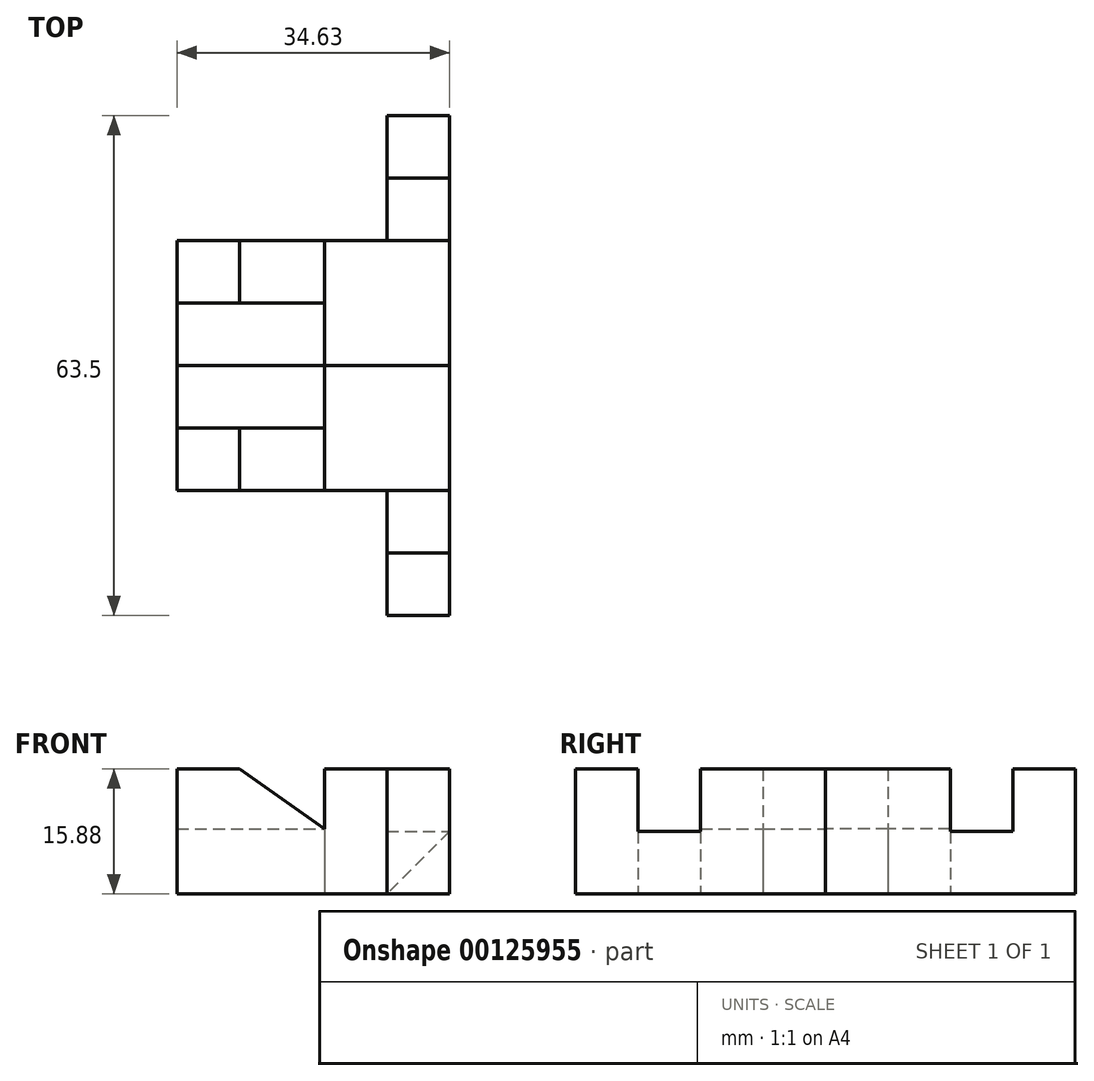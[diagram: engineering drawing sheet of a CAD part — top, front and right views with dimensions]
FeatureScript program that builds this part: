
annotation { "Feature Type Name" : "Feature", "Feature Type Description" : "" }
export const myFeature = defineFeature(function(context is Context, id is Id, definition is map)
    precondition{}
    {
        {
            var Q0;
            Q0=qCreatedBy(makeId("Top.planeOp"),FACE);
            var sketch = newSketch(context, id + "F0", { "sketchPlane" : qUnion([Q0])});
            skLineSegment(sketch, "E0.bottom", {"start": v(0, 0) * mm, "end": v(34.63, 0) * mm});
            skLineSegment(sketch, "E0.right", {"start": v(34.63, 0) * mm, "end": v(34.63, 31.75) * mm});
            skLineSegment(sketch, "E1", {"start": v(0, 15.88) * mm, "end": v(34.63, 15.88) * mm});
            skLineSegment(sketch, "E2", {"start": v(7.94, 15.88) * mm, "end": v(7.94, 7.94) * mm});
            skLineSegment(sketch, "E3", {"start": v(0, 15.88) * mm, "end": v(0, 0) * mm});
            skLineSegment(sketch, "E4", {"start": v(26.7, 31.75) * mm, "end": v(34.63, 31.75) * mm});
            skLineSegment(sketch, "E5", {"start": v(26.7, 23.81) * mm, "end": v(34.63, 23.81) * mm});
            skLineSegment(sketch, "E6", {"start": v(18.75, 15.88) * mm, "end": v(18.75, 0) * mm});
            skLineSegment(sketch, "E7", {"start": v(26.7, 31.75) * mm, "end": v(26.7, 15.88) * mm});
            skLineSegment(sketch, "E8", {"start": v(0, 7.94) * mm, "end": v(18.75, 7.94) * mm});
            skLineSegment(sketch, "E9", {"start": v(0, -6.14) * mm, "end": v(62.24, -6.14) * mm});
            skSolve(sketch);
        }
        {
            var Q0;
            {var subQ1=sQuery(id+"F0.wireOp",EDGE,"E0.right");var subQ4=sQuery(id+"F0.wireOp",EDGE,"E0.bottom");var subQ5=makeQuery(id+"F0.imprint","INTERSECT",VERTEX,{"derivedFrom":[subQ4,subQ1]});Q0=makeQuery(id+"F0.imprint","IMPRINT",FACE,{"disambiguationData":[TD([[makeQuery(id+"F0.imprint","IMPRINT",EDGE,{"disambiguationData":[TD([[subQ5,1.0]])],"derivedFrom":subQ4}),1.0]])]});}
            var Q1;
            {var subQ3=sQuery(id+"F0.wireOp",EDGE,"E2");Q1=makeQuery(id+"F0.imprint","IMPRINT",FACE,{"disambiguationData":[TD([[makeQuery(id+"F0.imprint","IMPRINT",EDGE,{"derivedFrom":subQ3}),-1.0]])]});}
            var Q2;
            {var subQ0=sQuery(id+"F0.wireOp",EDGE,"E4");Q2=makeQuery(id+"F0.imprint","IMPRINT",FACE,{"disambiguationData":[TD([[makeQuery(id+"F0.imprint","IMPRINT",EDGE,{"derivedFrom":subQ0}),-1.0]])]});}
            var Q3;
            {var subQ0=sQuery(id+"F0.wireOp",EDGE,"E2");Q3=makeQuery(id+"F0.imprint","IMPRINT",FACE,{"disambiguationData":[TD([[makeQuery(id+"F0.imprint","IMPRINT",EDGE,{"derivedFrom":subQ0}),1.0]])]});}
            var Q4;
            {var subQ3=sQuery(id+"F0.wireOp",EDGE,"E5");Q4=makeQuery(id+"F0.imprint","IMPRINT",FACE,{"disambiguationData":[TD([[makeQuery(id+"F0.imprint","IMPRINT",EDGE,{"derivedFrom":subQ3}),-1.0]])]});}
            extrude(context, id + "F1", {"entities" : qUnion([Q0, Q1, Q2, Q3, Q4]), "depth" : 15.88 * mm});
        }
        {
            var Q0;
            {var subQ1=sQuery(id+"F0.wireOp",EDGE,"E0.bottom");var subQ5=sQuery(id+"F0.wireOp",EDGE,"E3");var subQ6=makeQuery(id+"F0.imprint","INTERSECT",VERTEX,{"derivedFrom":[subQ1,subQ5]});Q0=makeQuery(id+"F0.imprint","IMPRINT",FACE,{"disambiguationData":[TD([[makeQuery(id+"F0.imprint","IMPRINT",EDGE,{"disambiguationData":[TD([[subQ6,-1.0]])],"derivedFrom":subQ1}),1.0]])]});}
            extrude(context, id + "F2", {"entities" : qUnion([Q0]), "depth" : 8.25 * mm});
        }
        {
            var Q0;
            Q0=makeQuery(id+"F1.opExtrude","SWEPT_FACE",FACE,{"disambiguationData":[OSD([sQuery(id+"F0.wireOp",EDGE,"E8")])]});
            var sketch = newSketch(context, id + "F3", { "sketchPlane" : qUnion([Q0])});
            skLineSegment(sketch, "E10.0", {"start": v(0, 15.88) * mm, "end": v(18.75, 15.88) * mm});
            skLineSegment(sketch, "E11.0", {"start": v(0, 8.26) * mm, "end": v(18.75, 8.26) * mm});
            skLineSegment(sketch, "E12", {"start": v(7.94, 15.88) * mm, "end": v(7.94, 8.26) * mm});
            skLineSegment(sketch, "E13", {"start": v(7.94, 15.88) * mm, "end": v(18.75, 8.26) * mm});
            skSolve(sketch);
        }
        {
            var Q0;
            {var subQ3=sQuery(id+"F3.wireOp",EDGE,"E13");Q0=makeQuery(id+"F3.imprint","IMPRINT",FACE,{"disambiguationData":[TD([[makeQuery(id+"F3.imprint","IMPRINT",EDGE,{"derivedFrom":subQ3}),1.0]])]});}
            extrude(context, id + "F4", {"entities" : qUnion([Q0]), "operationType" : NewBodyOperationType.REMOVE, "oppositeDirection" : true, "depth" : 25.4 * mm});
        }
        {
            var Q0;
            Q0=makeQuery(id+"F1.opExtrude","SWEPT_FACE",FACE,{"disambiguationData":[OSD([sQuery(id+"F0.wireOp",EDGE,"E0.right")])]});
            var sketch = newSketch(context, id + "F5", { "sketchPlane" : qUnion([Q0])});
            skLineSegment(sketch, "E14.0", {"start": v(31.75, 0) * mm, "end": v(15.87, 0) * mm});
            skLineSegment(sketch, "E15.0", {"start": v(0, 15.88) * mm, "end": v(31.75, 15.88) * mm});
            skLineSegment(sketch, "E16", {"start": v(15.87, 0) * mm, "end": v(15.87, 15.88) * mm});
            skLineSegment(sketch, "E17", {"start": v(23.81, 15.88) * mm, "end": v(23.81, 0) * mm});
            skLineSegment(sketch, "E18", {"start": v(15.87, 7.94) * mm, "end": v(23.81, 7.94) * mm});
            skSolve(sketch);
        }
        {
            var Q0;
            {var subQ5=sQuery(id+"F5.wireOp",EDGE,"E18");Q0=makeQuery(id+"F5.imprint","IMPRINT",FACE,{"disambiguationData":[TD([[makeQuery(id+"F5.imprint","IMPRINT",EDGE,{"derivedFrom":subQ5}),1.0]])]});}
            extrude(context, id + "F6", {"entities" : qUnion([Q0]), "operationType" : NewBodyOperationType.REMOVE, "oppositeDirection" : true, "depth" : 25.4 * mm});
        }
        {
            var Q0;
            Q0=makeQuery(id+"F1.opExtrude","SWEPT_BODY",BODY,{"disambiguationData":[OSD([sQuery(id+"F0.wireOp",EDGE,"E0.bottom"),sQuery(id+"F0.wireOp",EDGE,"E0.right"),sQuery(id+"F0.wireOp",EDGE,"E1"),sQuery(id+"F0.wireOp",EDGE,"E3"),sQuery(id+"F0.wireOp",EDGE,"E4"),sQuery(id+"F0.wireOp",EDGE,"E6"),sQuery(id+"F0.wireOp",EDGE,"E7"),sQuery(id+"F0.wireOp",EDGE,"E8")])]});
            var Q1;
            Q1=makeQuery(id+"F2.opExtrude","SWEPT_BODY",BODY,{"disambiguationData":[OSD([sQuery(id+"F0.wireOp",EDGE,"E0.bottom"),sQuery(id+"F0.wireOp",EDGE,"E3"),sQuery(id+"F0.wireOp",EDGE,"E6"),sQuery(id+"F0.wireOp",EDGE,"E8")])]});
            var Q2;
            Q2=qCreatedBy(makeId("Front.planeOp"),FACE);
            mirror(context, id + "F7", {"entities" : qUnion([Q0, Q1]), "mirrorPlane" : qUnion([Q2])});
        }
        {
            var Q0;
            Q0=makeQuery(id+"F7.opPattern","COPY",FACE,{"derivedFrom":makeQuery(id+"F6.boolean.opBoolean","COPY",FACE,{"derivedFrom":makeQuery(id+"F6.opExtrude","SWEPT_FACE",FACE,{"disambiguationData":[OSD([sQuery(id+"F5.wireOp",EDGE,"E18")])]})}),"instanceName":"1"});
            extrude(context, id + "F8", {"entities" : qUnion([Q0]), "operationType" : NewBodyOperationType.REMOVE, "oppositeDirection" : true, "depth" : 25 * mm});
        }
        {
            var Q0;
            {var subQ0=sQuery(id+"F5.wireOp",EDGE,"E17");Q0=makeQuery(id+"F8.boolean.opBoolean","MERGE",FACE,{"derivedFrom":[makeQuery(id+"F7.opPattern","COPY",FACE,{"derivedFrom":makeQuery(id+"F6.boolean.opBoolean","COPY",FACE,{"derivedFrom":makeQuery(id+"F6.opExtrude","SWEPT_FACE",FACE,{"disambiguationData":[OSD([subQ0])]})}),"instanceName":"1"}),makeQuery(id+"F8.opExtrude","SWEPT_FACE",FACE,{"disambiguationData":[OSD([subQ0,sQuery(id+"F5.wireOp",EDGE,"E18")])]})]});}
            var sketch = newSketch(context, id + "F9", { "sketchPlane" : qUnion([Q0])});
            skLineSegment(sketch, "E19", {"start": v(-34.63, 7.94) * mm, "end": v(-26.7, 7.94) * mm});
            skLineSegment(sketch, "E20", {"start": v(-34.63, 7.94) * mm, "end": v(-26.7, 0) * mm});
            skSolve(sketch);
        }
        {
            var Q0;
            {var subQ0=sQuery(id+"F9.wireOp",EDGE,"E20");Q0=makeQuery(id+"F9.imprint","IMPRINT",FACE,{"disambiguationData":[TD([[makeQuery(id+"F9.imprint","IMPRINT",EDGE,{"derivedFrom":subQ0}),-1.0]])]});}
            extrude(context, id + "F10", {"entities" : qUnion([Q0]), "operationType" : NewBodyOperationType.ADD, "depth" : 7.98 * mm});
        }
    });
